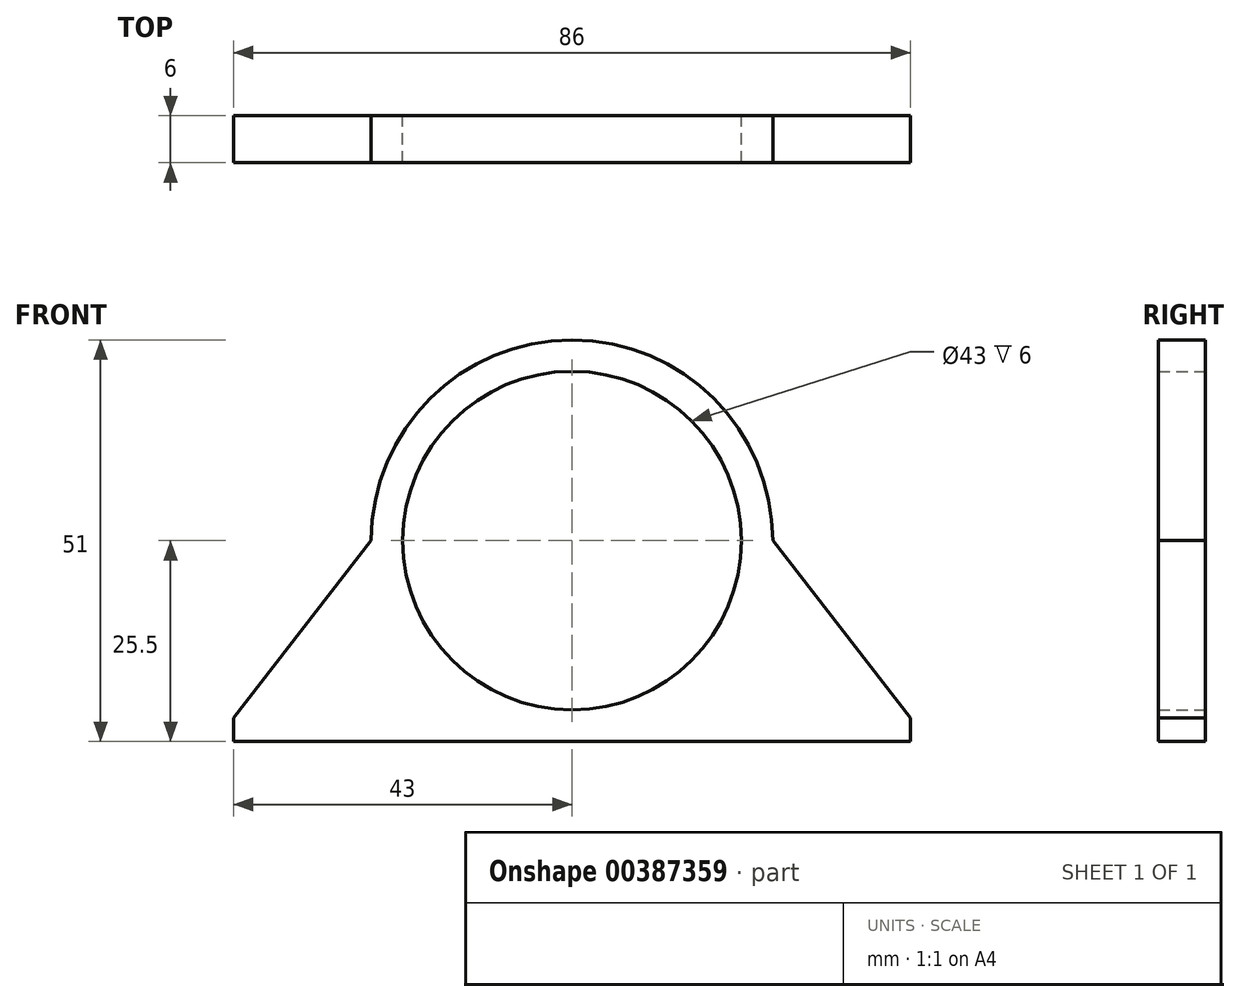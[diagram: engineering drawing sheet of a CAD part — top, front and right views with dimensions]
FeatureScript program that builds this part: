
annotation { "Feature Type Name" : "Feature", "Feature Type Description" : "" }
export const myFeature = defineFeature(function(context is Context, id is Id, definition is map)
    precondition{}
    {
        {
            var Q0;
            Q0=qCreatedBy(makeId("Front.planeOp"),FACE);
            var sketch = newSketch(context, id + "F0", { "sketchPlane" : qUnion([Q0])});
            skPoint(sketch, "E0", {"position": v(0, 0) * mm});
            skCircle(sketch, "E1", {"center": v(0, 0) * mm, "radius": 21.5 * mm});
            skCircle(sketch, "E2", {"center": v(0, 0) * mm, "radius": 25.5 * mm, "construction": true});
            skPoint(sketch, "E3", {"position": v(0, -25.5) * mm});
            skPoint(sketch, "E4", {"position": v(-43, -25.5) * mm});
            skPoint(sketch, "E5", {"position": v(-43, -22.5) * mm});
            skPoint(sketch, "E6", {"position": v(43, -25.5) * mm});
            skPoint(sketch, "E7", {"position": v(43, -22.5) * mm});
            skPoint(sketch, "E8", {"position": v(-25.5, 0) * mm});
            skPoint(sketch, "E9", {"position": v(25.5, 0) * mm});
            skLineSegment(sketch, "E10", {"start": v(-43, -25.5) * mm, "end": v(43, -25.5) * mm});
            skLineSegment(sketch, "E11", {"start": v(43, -25.5) * mm, "end": v(43, -22.5) * mm});
            skLineSegment(sketch, "E12", {"start": v(43, -22.5) * mm, "end": v(25.5, 0) * mm});
            skLineSegment(sketch, "E13", {"start": v(-43, -25.5) * mm, "end": v(-43, -22.5) * mm});
            skLineSegment(sketch, "E14", {"start": v(-43, -22.5) * mm, "end": v(-25.5, 0) * mm});
            skArc(sketch, "E15", {"start": v(25.5, 0) * mm, "mid": v(0, 25.5) * mm, "end": v(-25.5, 0) * mm});
            skSolve(sketch);
        }
        {
            var Q0;
            Q0=makeQuery(id+"F0.imprint","IMPRINT",FACE,{"disambiguationData":[TD([[makeQuery(id+"F0.imprint","IMPRINT",EDGE,{"derivedFrom":sQuery(id+"F0.wireOp",EDGE,"E1")}),-1.0]])]});
            extrude(context, id + "F1", {"entities" : qUnion([Q0]), "depth" : 6 * mm, "offsetDistance" : 25 * mm});
        }
    });
